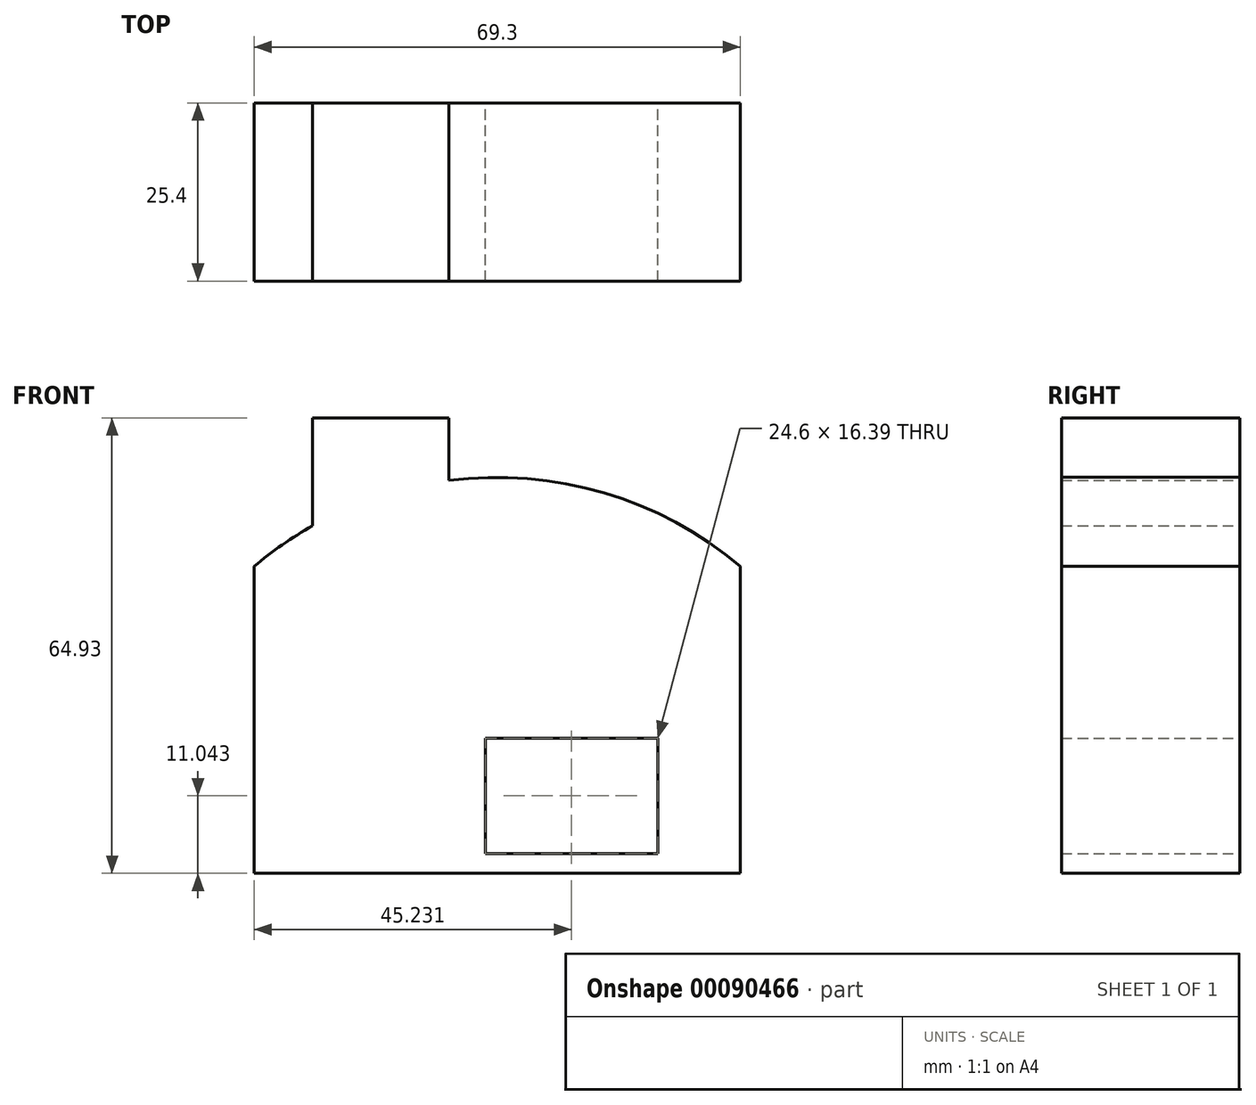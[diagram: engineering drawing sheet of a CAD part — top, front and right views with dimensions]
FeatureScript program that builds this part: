
annotation { "Feature Type Name" : "Feature", "Feature Type Description" : "" }
export const myFeature = defineFeature(function(context is Context, id is Id, definition is map)
    precondition{}
    {
        {
            var Q0;
            Q0=qCreatedBy(makeId("Front.planeOp"),FACE);
            var sketch = newSketch(context, id + "F0", { "sketchPlane" : qUnion([Q0])});
            skArc(sketch, "E0", {"start": v(69.3, 0) * mm, "mid": v(34.65, 12.7) * mm, "end": v(0, 0) * mm});
            skLineSegment(sketch, "E1", {"start": v(0, 0) * mm, "end": v(0, -43.75) * mm});
            skLineSegment(sketch, "E2.bottom", {"start": v(0, -43.75) * mm, "end": v(69.3, -43.75) * mm});
            skLineSegment(sketch, "E2.top", {"start": v(0, 0) * mm, "end": v(69.3, 0) * mm});
            skLineSegment(sketch, "E2.left", {"start": v(0, -43.75) * mm, "end": v(0, 0) * mm});
            skLineSegment(sketch, "E2.right", {"start": v(69.3, -43.75) * mm, "end": v(69.3, 0) * mm});
            skLineSegment(sketch, "E3.bottom", {"start": v(8.32, 0) * mm, "end": v(27.75, 0) * mm});
            skLineSegment(sketch, "E3.top", {"start": v(8.32, 21.18) * mm, "end": v(27.75, 21.18) * mm});
            skLineSegment(sketch, "E3.left", {"start": v(8.32, 0) * mm, "end": v(8.32, 21.18) * mm});
            skLineSegment(sketch, "E3.right", {"start": v(27.75, 0) * mm, "end": v(27.75, 21.18) * mm});
            skLineSegment(sketch, "E4.bottom", {"start": v(32.93, -40.9) * mm, "end": v(57.53, -40.9) * mm});
            skLineSegment(sketch, "E4.top", {"start": v(32.93, -24.51) * mm, "end": v(57.53, -24.51) * mm});
            skLineSegment(sketch, "E4.left", {"start": v(32.93, -40.9) * mm, "end": v(32.93, -24.51) * mm});
            skLineSegment(sketch, "E4.right", {"start": v(57.53, -40.9) * mm, "end": v(57.53, -24.51) * mm});
            skSolve(sketch);
        }
        {
            var Q0;
            Q0 = qSketchRegion(id + "F0", true);
            extrude(context, id + "F1", {"entities" : qUnion([Q0]), "depth" : 25.4 * mm});
        }
    });
